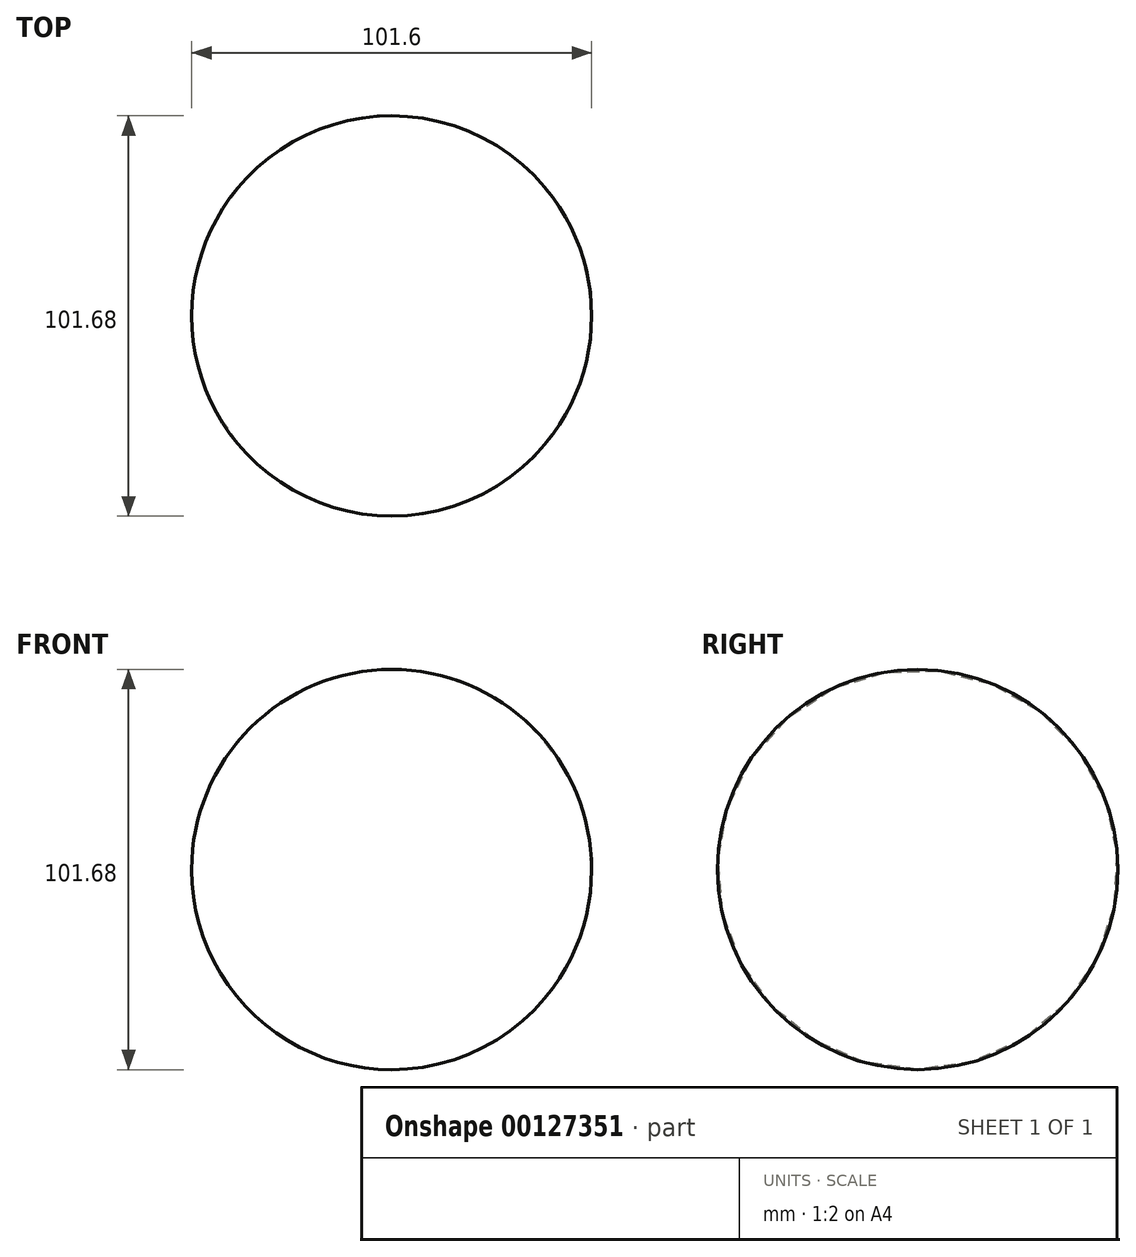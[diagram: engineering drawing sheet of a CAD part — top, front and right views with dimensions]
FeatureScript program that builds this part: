
annotation { "Feature Type Name" : "Feature", "Feature Type Description" : "" }
export const myFeature = defineFeature(function(context is Context, id is Id, definition is map)
    precondition{}
    {
        {
            var Q0;
            Q0=qCreatedBy(makeId("Front.planeOp"),FACE);
            var sketch = newSketch(context, id + "F0", { "sketchPlane" : qUnion([Q0])});
            skLineSegment(sketch, "E0", {"start": v(-46.18, 0) * mm, "end": v(55.42, 0) * mm});
            skArc(sketch, "E1", {"start": v(55.42, 0) * mm, "mid": v(4.62, 50.84) * mm, "end": v(-46.18, 0) * mm});
            skSolve(sketch);
        }
        {
            var Q0;
            Q0 = qSketchRegion(id + "F0", true);
            var Q1;
            Q1=sQuery(id+"F0.wireOp",EDGE,"E0");
            revolve(context, id + "F1", {"entities" : qUnion([Q0]), "axis" : qUnion([Q1]), "revolveType" : RevolveType.FULL});
        }
    });
